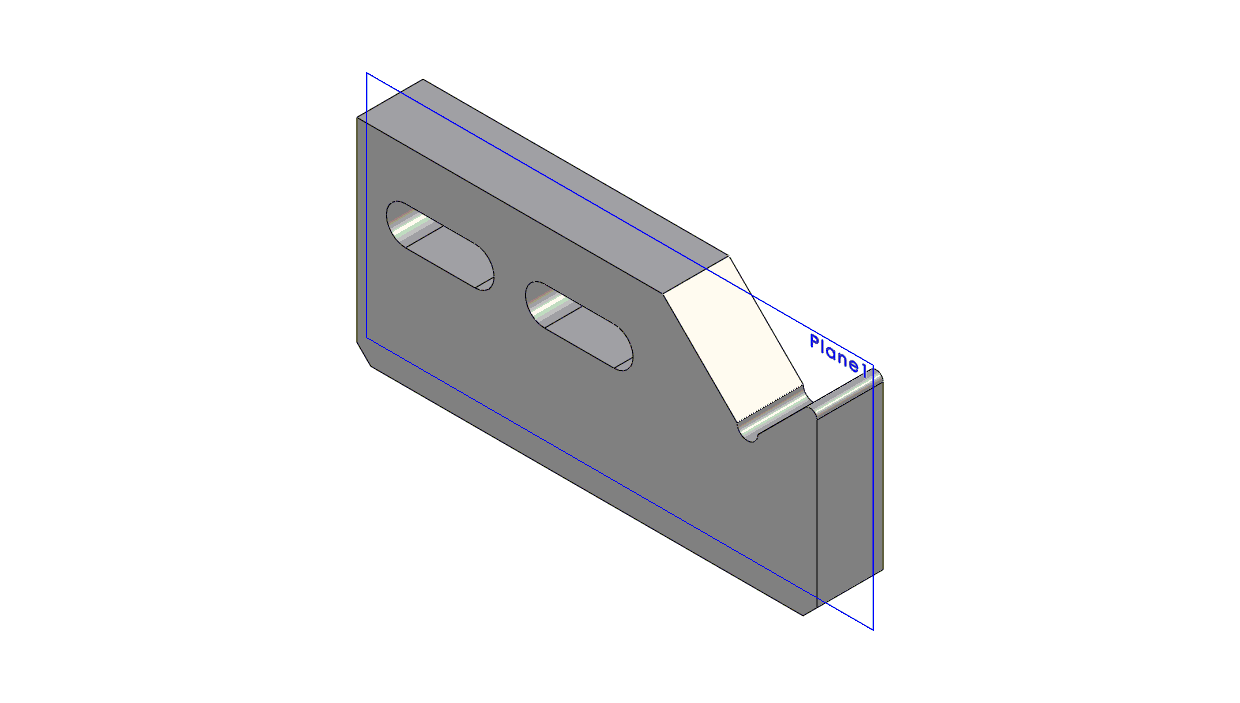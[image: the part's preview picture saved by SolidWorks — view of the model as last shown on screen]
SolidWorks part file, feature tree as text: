
SOLIDWORKS PART (.sldprt)
format: sldprt  version: not decoded by parser v0  size: 214,016 bytes
history: native  units: mm
features: sketch x2, chamfer x2, material x1, extrude x1, fillet x1, plane x1, cut_revolve x1 (+16 scaffold rows collapsed)
feature tree (25):
  scaffold x16  (default folders/planes/origin — collapsed)
  material  "Plain Carbon Steel"
  sketch  "Sketch1"
  extrude  "Boss-Extrude1"  Depth=6mm
  fillet  "Fillet1"  Radius=1mm
  chamfer  "Chamfer1"  Distance=2mm Angle=45deg
  plane  "Plane1"
  sketch  "Sketch3"
  cut_revolve  "Cut-Revolve1"  Angle=360deg
  chamfer  "Chamfer2"  Distance=0.5mm Angle=45deg
decode coverage: 5 of 7 modeling features carry decoded parameters
note: suppression state not decoded; provenance and decode notes live in map.json
